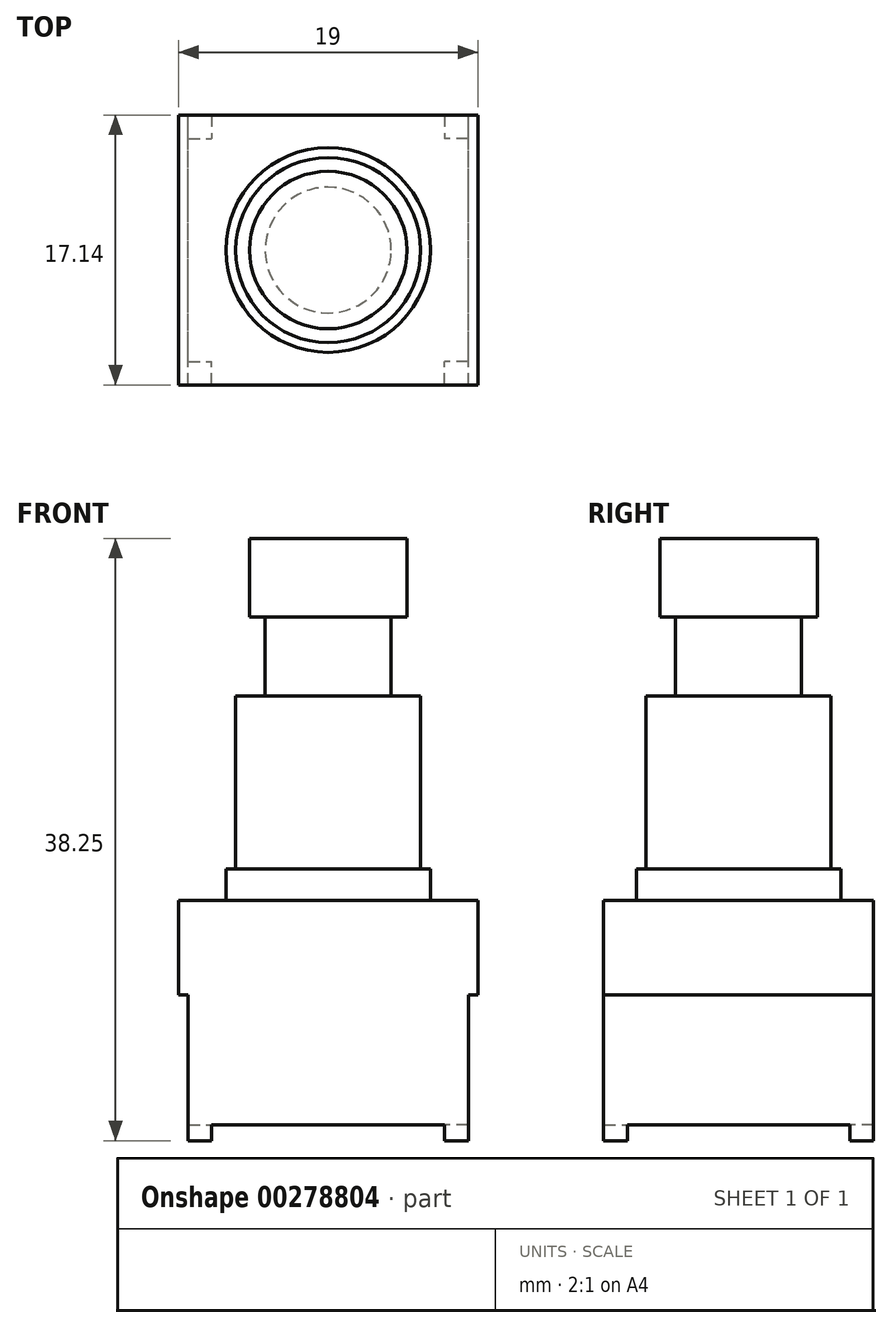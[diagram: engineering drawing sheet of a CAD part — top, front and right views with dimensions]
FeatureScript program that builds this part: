
annotation { "Feature Type Name" : "Feature", "Feature Type Description" : "" }
export const myFeature = defineFeature(function(context is Context, id is Id, definition is map)
    precondition{}
    {
        {
            var Q0;
            Q0=qCreatedBy(makeId("Top.planeOp"),FACE);
            var sketch = newSketch(context, id + "F0", { "sketchPlane" : qUnion([Q0])});
            skLineSegment(sketch, "E0.bottom", {"start": v(9.5, 8.58) * mm, "end": v(-9.5, 8.58) * mm});
            skLineSegment(sketch, "E0.top", {"start": v(9.5, -8.57) * mm, "end": v(-9.5, -8.57) * mm});
            skLineSegment(sketch, "E0.left", {"start": v(9.5, 8.58) * mm, "end": v(9.5, -8.57) * mm});
            skLineSegment(sketch, "E0.right", {"start": v(-9.5, 8.58) * mm, "end": v(-9.5, -8.57) * mm});
            skPoint(sketch, "E0.middle", {"position": v(0, 0) * mm});
            skSolve(sketch);
        }
        {
            var Q0;
            Q0 = qSketchRegion(id + "F0", true);
            extrude(context, id + "F1", {"entities" : qUnion([Q0]), "depth" : 6 * mm});
        }
        {
            var Q0;
            Q0=makeQuery(id+"F1.opExtrude","CAP_FACE",FACE,{"disambiguationData":[OSD([sQuery(id+"F0.wireOp",EDGE,"E0.bottom"),sQuery(id+"F0.wireOp",EDGE,"E0.top"),sQuery(id+"F0.wireOp",EDGE,"E0.left"),sQuery(id+"F0.wireOp",EDGE,"E0.right")])],"isStart":true});
            var sketch = newSketch(context, id + "F2", { "sketchPlane" : qUnion([Q0])});
            skLineSegment(sketch, "E1.bottom", {"start": v(8.9, 8.57) * mm, "end": v(-8.9, 8.57) * mm});
            skLineSegment(sketch, "E1.top", {"start": v(8.9, -8.57) * mm, "end": v(-8.9, -8.57) * mm});
            skLineSegment(sketch, "E1.left", {"start": v(8.9, 8.57) * mm, "end": v(8.9, -8.57) * mm});
            skLineSegment(sketch, "E1.right", {"start": v(-8.9, 8.57) * mm, "end": v(-8.9, -8.57) * mm});
            skPoint(sketch, "E1.middle", {"position": v(0, 0) * mm});
            skSolve(sketch);
        }
        {
            var Q0;
            Q0 = qSketchRegion(id + "F2", true);
            extrude(context, id + "F3", {"entities" : qUnion([Q0]), "operationType" : NewBodyOperationType.ADD, "depth" : 8.25 * mm});
        }
        {
            var Q0;
            Q0=makeQuery(id+"F3.opExtrude","CAP_FACE",FACE,{"disambiguationData":[OSD([sQuery(id+"F2.wireOp",EDGE,"E1.bottom"),sQuery(id+"F2.wireOp",EDGE,"E1.top"),sQuery(id+"F2.wireOp",EDGE,"E1.left"),sQuery(id+"F2.wireOp",EDGE,"E1.right")])],"isStart":false});
            var sketch = newSketch(context, id + "F4", { "sketchPlane" : qUnion([Q0])});
            skLineSegment(sketch, "E2.bottom", {"start": v(-8.9, 8.57) * mm, "end": v(-7.4, 8.57) * mm});
            skLineSegment(sketch, "E2.top", {"start": v(-8.9, 7.07) * mm, "end": v(-7.4, 7.07) * mm});
            skLineSegment(sketch, "E2.left", {"start": v(-8.9, 8.57) * mm, "end": v(-8.9, 7.07) * mm});
            skLineSegment(sketch, "E2.right", {"start": v(-7.4, 8.57) * mm, "end": v(-7.4, 7.07) * mm});
            skLineSegment(sketch, "E3.bottom", {"start": v(8.9, 8.57) * mm, "end": v(7.4, 8.57) * mm});
            skLineSegment(sketch, "E3.top", {"start": v(8.9, 7.07) * mm, "end": v(7.4, 7.07) * mm});
            skLineSegment(sketch, "E3.left", {"start": v(8.9, 8.57) * mm, "end": v(8.9, 7.07) * mm});
            skLineSegment(sketch, "E3.right", {"start": v(7.4, 8.57) * mm, "end": v(7.4, 7.07) * mm});
            skLineSegment(sketch, "E4.bottom", {"start": v(-8.9, -8.58) * mm, "end": v(-7.4, -8.58) * mm});
            skLineSegment(sketch, "E4.top", {"start": v(-8.9, -7.08) * mm, "end": v(-7.4, -7.08) * mm});
            skLineSegment(sketch, "E4.left", {"start": v(-8.9, -8.58) * mm, "end": v(-8.9, -7.08) * mm});
            skLineSegment(sketch, "E4.right", {"start": v(-7.4, -8.58) * mm, "end": v(-7.4, -7.08) * mm});
            skLineSegment(sketch, "E5.bottom", {"start": v(8.9, -8.58) * mm, "end": v(7.4, -8.58) * mm});
            skLineSegment(sketch, "E5.top", {"start": v(8.9, -7.08) * mm, "end": v(7.4, -7.08) * mm});
            skLineSegment(sketch, "E5.left", {"start": v(8.9, -8.58) * mm, "end": v(8.9, -7.08) * mm});
            skLineSegment(sketch, "E5.right", {"start": v(7.4, -8.58) * mm, "end": v(7.4, -7.08) * mm});
            skSolve(sketch);
        }
        {
            var Q0;
            Q0 = qSketchRegion(id + "F4", true);
            extrude(context, id + "F5", {"entities" : qUnion([Q0]), "operationType" : NewBodyOperationType.ADD, "depth" : 1 * mm});
        }
        {
            var Q0;
            Q0=makeQuery(id+"F1.opExtrude","CAP_FACE",FACE,{"disambiguationData":[OSD([sQuery(id+"F0.wireOp",EDGE,"E0.bottom"),sQuery(id+"F0.wireOp",EDGE,"E0.top"),sQuery(id+"F0.wireOp",EDGE,"E0.left"),sQuery(id+"F0.wireOp",EDGE,"E0.right")])],"isStart":false});
            var sketch = newSketch(context, id + "F6", { "sketchPlane" : qUnion([Q0])});
            skCircle(sketch, "E6", {"center": v(0, 0) * mm, "radius": 6.5 * mm});
            skSolve(sketch);
        }
        {
            var Q0;
            Q0 = qSketchRegion(id + "F6", true);
            extrude(context, id + "F7", {"entities" : qUnion([Q0]), "depth" : 2 * mm});
        }
        {
            var Q0;
            Q0=makeQuery(id+"F7.opExtrude","CAP_FACE",FACE,{"disambiguationData":[OSD([sQuery(id+"F6.wireOp",EDGE,"E6")])],"isStart":false});
            var sketch = newSketch(context, id + "F8", { "sketchPlane" : qUnion([Q0])});
            skCircle(sketch, "E7", {"center": v(0, 0) * mm, "radius": 5.88 * mm});
            skSolve(sketch);
        }
        {
            var Q0;
            Q0 = qSketchRegion(id + "F8", true);
            extrude(context, id + "F9", {"entities" : qUnion([Q0]), "operationType" : NewBodyOperationType.ADD, "depth" : 11 * mm});
        }
        {
            var Q0;
            Q0=makeQuery(id+"F9.opExtrude","CAP_FACE",FACE,{"disambiguationData":[OSD([sQuery(id+"F8.wireOp",EDGE,"E7")])],"isStart":false});
            var sketch = newSketch(context, id + "F10", { "sketchPlane" : qUnion([Q0])});
            skCircle(sketch, "E8", {"center": v(0, 0) * mm, "radius": 4 * mm});
            skSolve(sketch);
        }
        {
            var Q0;
            Q0 = qSketchRegion(id + "F10", true);
            extrude(context, id + "F11", {"entities" : qUnion([Q0]), "operationType" : NewBodyOperationType.ADD, "depth" : 5 * mm});
        }
        {
            var Q0;
            Q0=makeQuery(id+"F11.opExtrude","CAP_FACE",FACE,{"disambiguationData":[OSD([sQuery(id+"F10.wireOp",EDGE,"E8")])],"isStart":false});
            var sketch = newSketch(context, id + "F12", { "sketchPlane" : qUnion([Q0])});
            skCircle(sketch, "E9", {"center": v(0, 0) * mm, "radius": 5 * mm});
            skSolve(sketch);
        }
        {
            var Q0;
            Q0 = qSketchRegion(id + "F12", true);
            extrude(context, id + "F13", {"entities" : qUnion([Q0]), "operationType" : NewBodyOperationType.ADD, "depth" : 5 * mm});
        }
    });
